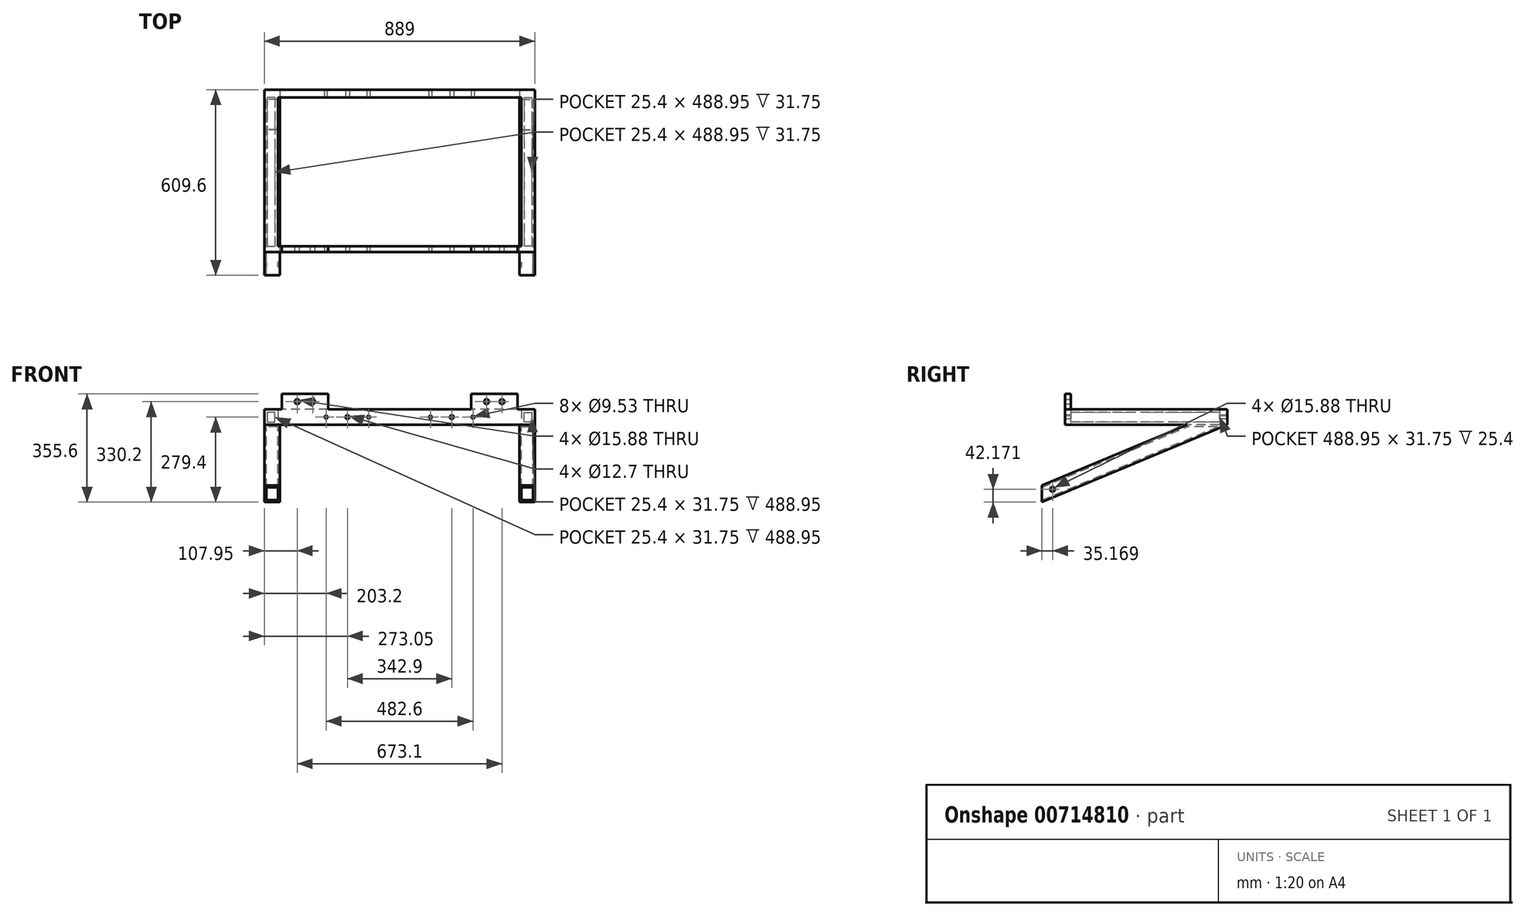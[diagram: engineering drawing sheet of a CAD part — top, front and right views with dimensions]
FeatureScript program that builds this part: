
annotation { "Feature Type Name" : "Feature", "Feature Type Description" : "" }
export const myFeature = defineFeature(function(context is Context, id is Id, definition is map)
    precondition{}
    {
        {
            var Q0;
            Q0=qCreatedBy(makeId("Top.planeOp"),FACE);
            var sketch = newSketch(context, id + "F0", { "sketchPlane" : qUnion([Q0])});
            skLineSegment(sketch, "E0", {"start": v(0, 0) * mm, "end": v(444.5, 0) * mm});
            skLineSegment(sketch, "E1", {"start": v(0, 0) * mm, "end": v(0, 19.05) * mm});
            skLineSegment(sketch, "E2", {"start": v(0, 19.05) * mm, "end": v(444.5, 19.05) * mm});
            skLineSegment(sketch, "E3", {"start": v(444.5, 19.05) * mm, "end": v(444.5, 0) * mm});
            skSolve(sketch);
        }
        {
            var Q0;
            Q0 = qSketchRegion(id + "F0", true);
            extrude(context, id + "F1", {"entities" : qUnion([Q0]), "depth" : 50.8 * mm, "offsetDistance" : 25.4 * mm});
        }
        {
            var Q0;
            Q0=makeQuery(id+"F1.opExtrude","CAP_FACE",FACE,{"disambiguationData":[OSD([sQuery(id+"F0.wireOp",EDGE,"E0"),sQuery(id+"F0.wireOp",EDGE,"E1"),sQuery(id+"F0.wireOp",EDGE,"E2"),sQuery(id+"F0.wireOp",EDGE,"E3")])],"isStart":false});
            var sketch = newSketch(context, id + "F2", { "sketchPlane" : qUnion([Q0])});
            skLineSegment(sketch, "E4", {"start": v(387.35, 19.05) * mm, "end": v(387.35, 0) * mm});
            skLineSegment(sketch, "E5", {"start": v(387.35, 0) * mm, "end": v(234.95, 0) * mm});
            skLineSegment(sketch, "E6", {"start": v(234.95, 0) * mm, "end": v(234.95, 19.05) * mm});
            skLineSegment(sketch, "E7", {"start": v(234.95, 19.05) * mm, "end": v(387.35, 19.05) * mm});
            skSolve(sketch);
        }
        {
            var Q0;
            Q0 = qSketchRegion(id + "F2", true);
            extrude(context, id + "F3", {"entities" : qUnion([Q0]), "operationType" : NewBodyOperationType.ADD, "depth" : 50.8 * mm, "offsetDistance" : 25.4 * mm});
        }
        {
            var Q0;
            Q0=makeQuery(id+"F3.boolean.opBoolean","MERGE",FACE,{"derivedFrom":[makeQuery(id+"F1.opExtrude","SWEPT_FACE",FACE,{"disambiguationData":[OSD([sQuery(id+"F0.wireOp",EDGE,"E2")])]}),makeQuery(id+"F3.opExtrude","SWEPT_FACE",FACE,{"disambiguationData":[OSD([sQuery(id+"F2.wireOp",EDGE,"E7")])]})]});
            var sketch = newSketch(context, id + "F4", { "sketchPlane" : qUnion([Q0])});
            skLineSegment(sketch, "E8", {"start": v(-444.5, 50.8) * mm, "end": v(-444.5, 0) * mm});
            skLineSegment(sketch, "E9.0", {"start": v(-409.58, 9.53) * mm, "end": v(-409.58, 41.27) * mm});
            skLineSegment(sketch, "E10.0", {"start": v(-409.58, 41.27) * mm, "end": v(-434.98, 41.27) * mm});
            skLineSegment(sketch, "E11.0", {"start": v(-434.98, 41.27) * mm, "end": v(-434.98, 9.52) * mm});
            skLineSegment(sketch, "E12.0", {"start": v(-434.98, 9.52) * mm, "end": v(-409.58, 9.53) * mm});
            skLineSegment(sketch, "E13", {"start": v(-400.05, 50.8) * mm, "end": v(-400.05, 0) * mm});
            skLineSegment(sketch, "E14", {"start": v(-444.5, 50.8) * mm, "end": v(-400.05, 50.8) * mm});
            skLineSegment(sketch, "E15", {"start": v(-444.5, 0) * mm, "end": v(-400.05, 0) * mm});
            skSolve(sketch);
        }
        {
            var Q0;
            Q0 = qSketchRegion(id + "F4", true);
            extrude(context, id + "F5", {"entities" : qUnion([Q0]), "operationType" : NewBodyOperationType.ADD, "depth" : 488.95 * mm, "offsetDistance" : 25.4 * mm});
        }
        {
            var Q0;
            Q0=makeQuery(id+"F5.opExtrude","CAP_FACE",FACE,{"disambiguationData":[OSD([sQuery(id+"F4.wireOp",EDGE,"FWYuwISs-E6if-5kSW-0V8y-lrcbosfp9W8B"),sQuery(id+"F4.wireOp",EDGE,"E8"),sQuery(id+"F4.wireOp",EDGE,"6qbx7gXe-cqjZ-glUW-nPfE-zQhVoUlrfZX7"),sQuery(id+"F4.wireOp",EDGE,"8mQaY77S-jLiu-1Mix-MAS4-rNiHFhKHHUlm"),sQuery(id+"F4.wireOp",EDGE,"E9.0"),sQuery(id+"F4.wireOp",EDGE,"E10.0"),sQuery(id+"F4.wireOp",EDGE,"E11.0"),sQuery(id+"F4.wireOp",EDGE,"E12.0")])],"isStart":false});
            var sketch = newSketch(context, id + "F6", { "sketchPlane" : qUnion([Q0])});
            skLineSegment(sketch, "E16", {"start": v(-444.5, 0) * mm, "end": v(0, 0) * mm});
            skLineSegment(sketch, "E17", {"start": v(0, 0) * mm, "end": v(0, 0) * mm});
            skLineSegment(sketch, "E18", {"start": v(0, 0) * mm, "end": v(-444.5, 0) * mm});
            skLineSegment(sketch, "E19", {"start": v(-444.5, 0) * mm, "end": v(-444.5, 0) * mm});
            skLineSegment(sketch, "E20", {"start": v(-444.5, 0) * mm, "end": v(-444.5, 50.8) * mm});
            skLineSegment(sketch, "E21", {"start": v(-444.5, 50.8) * mm, "end": v(0, 50.8) * mm});
            skLineSegment(sketch, "E22", {"start": v(0, 50.8) * mm, "end": v(0, 0) * mm});
            skSolve(sketch);
        }
        {
            var Q0;
            Q0 = qSketchRegion(id + "F6", true);
            extrude(context, id + "F7", {"entities" : qUnion([Q0]), "operationType" : NewBodyOperationType.ADD, "depth" : 25.4 * mm, "offsetDistance" : 25.4 * mm});
        }
        {
            var Q0;
            {var subQ2=sQuery(id+"F0.wireOp",EDGE,"E2");var subQ3=sQuery(id+"F0.wireOp",EDGE,"E1");var subQ5=sQuery(id+"F2.wireOp",EDGE,"E7");Q0=makeQuery(id+"F5.boolean.opBoolean","SPLIT",FACE,{"disambiguationData":[TD([makeQuery(id+"F1.opExtrude","SWEPT_FACE",FACE,{"disambiguationData":[OSD([subQ3])]})])],"derivedFrom":makeQuery(id+"F3.boolean.opBoolean","MERGE",FACE,{"derivedFrom":[makeQuery(id+"F1.opExtrude","SWEPT_FACE",FACE,{"disambiguationData":[OSD([subQ2])]}),makeQuery(id+"F3.opExtrude","SWEPT_FACE",FACE,{"disambiguationData":[OSD([subQ5])]})]})});}
            var sketch = newSketch(context, id + "F8", { "sketchPlane" : qUnion([Q0])});
            skLineSegment(sketch, "E23", {"start": v(-387.35, 101.6) * mm, "end": v(-387.35, 76.2) * mm});
            skLineSegment(sketch, "E24", {"start": v(-387.35, 76.2) * mm, "end": v(-336.55, 76.2) * mm});
            skLineSegment(sketch, "E25", {"start": v(-336.55, 76.2) * mm, "end": v(-285.75, 76.2) * mm});
            skCircle(sketch, "E26", {"center": v(-336.55, 76.2) * mm, "radius": 7.94 * mm});
            skCircle(sketch, "E27", {"center": v(-285.75, 76.2) * mm, "radius": 7.94 * mm});
            skSolve(sketch);
        }
        {
            var Q0;
            Q0 = qSketchRegion(id + "F8", true);
            extrude(context, id + "F9", {"entities" : qUnion([Q0]), "operationType" : NewBodyOperationType.REMOVE, "oppositeDirection" : true, "depth" : 25.4 * mm, "offsetDistance" : 25.4 * mm});
        }
        {
            var Q0;
            Q0=makeQuery(id+"F3.boolean.opBoolean","MERGE",FACE,{"derivedFrom":[makeQuery(id+"F1.opExtrude","SWEPT_FACE",FACE,{"disambiguationData":[OSD([sQuery(id+"F0.wireOp",EDGE,"E0")])]}),makeQuery(id+"F3.opExtrude","SWEPT_FACE",FACE,{"disambiguationData":[OSD([sQuery(id+"F2.wireOp",EDGE,"E5")])]})]});
            var sketch = newSketch(context, id + "F10", { "sketchPlane" : qUnion([Q0])});
            skLineSegment(sketch, "E28", {"start": v(234.95, 50.8) * mm, "end": v(234.95, 25.4) * mm});
            skPoint(sketch, "E28.endSnap0", {"position": v(0, 25.4) * mm});
            skLineSegment(sketch, "E29", {"start": v(234.95, 25.4) * mm, "end": v(171.45, 25.4) * mm});
            skCircle(sketch, "E30", {"center": v(171.45, 25.4) * mm, "radius": 6.35 * mm});
            skSolve(sketch);
        }
        {
            var Q0;
            Q0 = qSketchRegion(id + "F10", true);
            extrude(context, id + "F11", {"entities" : qUnion([Q0]), "operationType" : NewBodyOperationType.REMOVE, "oppositeDirection" : true, "depth" : 25.4 * mm, "offsetDistance" : 25.4 * mm});
        }
        {
            var Q0;
            Q0=makeQuery(id+"F7.boolean.opBoolean","MERGE",FACE,{"derivedFrom":[makeQuery(id+"F5.boolean.opBoolean","MERGE",FACE,{"derivedFrom":[makeQuery(id+"F1.opExtrude","SWEPT_FACE",FACE,{"disambiguationData":[OSD([sQuery(id+"F0.wireOp",EDGE,"E3")])]}),makeQuery(id+"F5.opExtrude","SWEPT_FACE",FACE,{"disambiguationData":[OSD([sQuery(id+"F4.wireOp",EDGE,"E8")])]})]}),makeQuery(id+"F7.opExtrude","SWEPT_FACE",FACE,{"disambiguationData":[OSD([sQuery(id+"F6.wireOp",EDGE,"E19")])]})]});
            var sketch = newSketch(context, id + "F12", { "sketchPlane" : qUnion([Q0])});
            skLineSegment(sketch, "E31", {"start": v(0, 0) * mm, "end": v(-76.2, 0) * mm});
            skLineSegment(sketch, "E32", {"start": v(-76.2, -198.97) * mm, "end": v(-76.2, -254) * mm});
            skLineSegment(sketch, "E33", {"start": v(-76.2, -254) * mm, "end": v(533.4, 0) * mm});
            skLineSegment(sketch, "E34.0", {"start": v(-76.2, -198.97) * mm, "end": v(401.32, 0) * mm});
            skLineSegment(sketch, "E35", {"start": v(533.4, 0) * mm, "end": v(401.32, 0) * mm});
            skSolve(sketch);
        }
        {
            var Q0;
            Q0 = qSketchRegion(id + "F12", true);
            extrude(context, id + "F13", {"entities" : qUnion([Q0]), "oppositeDirection" : true, "depth" : 50.8 * mm, "offsetDistance" : 25.4 * mm});
        }
        {
            var Q0;
            Q0=makeQuery(id+"F13.opExtrude","SWEPT_FACE",FACE,{"disambiguationData":[OSD([sQuery(id+"F12.wireOp",EDGE,"E32")])]});
            shell(context, id + "F14", {"entities" : qUnion([Q0]), "thickness" : 6.35 * mm});
        }
        {
            var Q0;
            Q0=makeQuery(id+"F13.opExtrude","CAP_FACE",FACE,{"disambiguationData":[OSD([sQuery(id+"F12.wireOp",EDGE,"E32"),sQuery(id+"F12.wireOp",EDGE,"E33"),sQuery(id+"F12.wireOp",EDGE,"E34.0"),sQuery(id+"F12.wireOp",EDGE,"E35")])],"isStart":true});
            var sketch = newSketch(context, id + "F15", { "sketchPlane" : qUnion([Q0])});
            skLineSegment(sketch, "E36", {"start": v(-76.2, -226.48) * mm, "end": v(467.36, 0) * mm});
            skCircle(sketch, "E37", {"center": v(-41.03, -211.83) * mm, "radius": 7.94 * mm});
            skSolve(sketch);
        }
        {
            var Q0;
            Q0 = qSketchRegion(id + "F15", true);
            extrude(context, id + "F16", {"entities" : qUnion([Q0]), "operationType" : NewBodyOperationType.REMOVE, "endBound" : BoundingType.THROUGH_ALL, "oppositeDirection" : true, "depth" : 25.4 * mm, "offsetDistance" : 25.4 * mm});
        }
        {
            var Q0;
            Q0 = qSketchRegion(id + "F15", true);
            extrude(context, id + "F17", {"entities" : qUnion([Q0]), "operationType" : NewBodyOperationType.REMOVE, "endBound" : BoundingType.THROUGH_ALL, "oppositeDirection" : true, "depth" : 25.4 * mm, "offsetDistance" : 25.4 * mm});
        }
        {
            var Q0;
            Q0=makeQuery(id+"F7.opExtrude","CAP_FACE",FACE,{"disambiguationData":[OSD([sQuery(id+"F6.wireOp",EDGE,"E16"),sQuery(id+"F6.wireOp",EDGE,"E17"),sQuery(id+"F6.wireOp",EDGE,"E18"),sQuery(id+"F6.wireOp",EDGE,"E19")])],"isStart":false});
            var sketch = newSketch(context, id + "F18", { "sketchPlane" : qUnion([Q0])});
            skCircle(sketch, "E38", {"center": v(-241.3, 25.4) * mm, "radius": 4.76 * mm});
            skCircle(sketch, "E39", {"center": v(-101.6, 25.4) * mm, "radius": 4.76 * mm});
            skSolve(sketch);
        }
        {
            var Q0;
            {var subQ4=sQuery(id+"F6.wireOp",EDGE,"E21");var subQ5=sQuery(id+"F6.wireOp",EDGE,"E18");var subQ6=sQuery(id+"F6.wireOp",EDGE,"E22");Q0=makeQuery(id+"F7.boolean.opBoolean","SPLIT",FACE,{"disambiguationData":[TD([makeQuery(id+"F5.opExtrude","SWEPT_FACE",FACE,{"disambiguationData":[OSD([sQuery(id+"F4.wireOp",EDGE,"E13")])]})])],"derivedFrom":makeQuery(id+"F7.opExtrude","CAP_FACE",FACE,{"disambiguationData":[OSD([subQ5,sQuery(id+"F6.wireOp",EDGE,"E20"),subQ4,subQ6])],"isStart":true})});}
            var sketch = newSketch(context, id + "F19", { "sketchPlane" : qUnion([Q0])});
            skCircle(sketch, "E40", {"center": v(171.45, 25.4) * mm, "radius": 6.35 * mm});
            skSolve(sketch);
        }
        {
            var Q0;
            Q0 = qSketchRegion(id + "F19", true);
            extrude(context, id + "F20", {"entities" : qUnion([Q0]), "operationType" : NewBodyOperationType.REMOVE, "oppositeDirection" : true, "depth" : 25.4 * mm, "offsetDistance" : 25.4 * mm});
        }
        {
            var Q0;
            Q0 = qSketchRegion(id + "F18", true);
            extrude(context, id + "F21", {"entities" : qUnion([Q0]), "operationType" : NewBodyOperationType.REMOVE, "endBound" : BoundingType.THROUGH_ALL, "oppositeDirection" : true, "depth" : 25.4 * mm, "offsetDistance" : 25.4 * mm});
        }
        {
            var Q0;
            Q0=makeQuery(id+"F13.opExtrude","SWEPT_BODY",BODY,{"disambiguationData":[OSD([sQuery(id+"F12.wireOp",EDGE,"E32"),sQuery(id+"F12.wireOp",EDGE,"E33"),sQuery(id+"F12.wireOp",EDGE,"E34.0"),sQuery(id+"F12.wireOp",EDGE,"E35")])]});
            var Q1;
            Q1=makeQuery(id+"F1.opExtrude","SWEPT_BODY",BODY,{"disambiguationData":[OSD([sQuery(id+"F0.wireOp",EDGE,"E0"),sQuery(id+"F0.wireOp",EDGE,"E1"),sQuery(id+"F0.wireOp",EDGE,"E2"),sQuery(id+"F0.wireOp",EDGE,"E3")])]});
            var Q2;
            Q2=qCreatedBy(makeId("Right.planeOp"),FACE);
            mirror(context, id + "F22", {"operationType" : NewBodyOperationType.ADD, "entities" : qUnion([Q0, Q1]), "mirrorPlane" : qUnion([Q2])});
        }
    });
